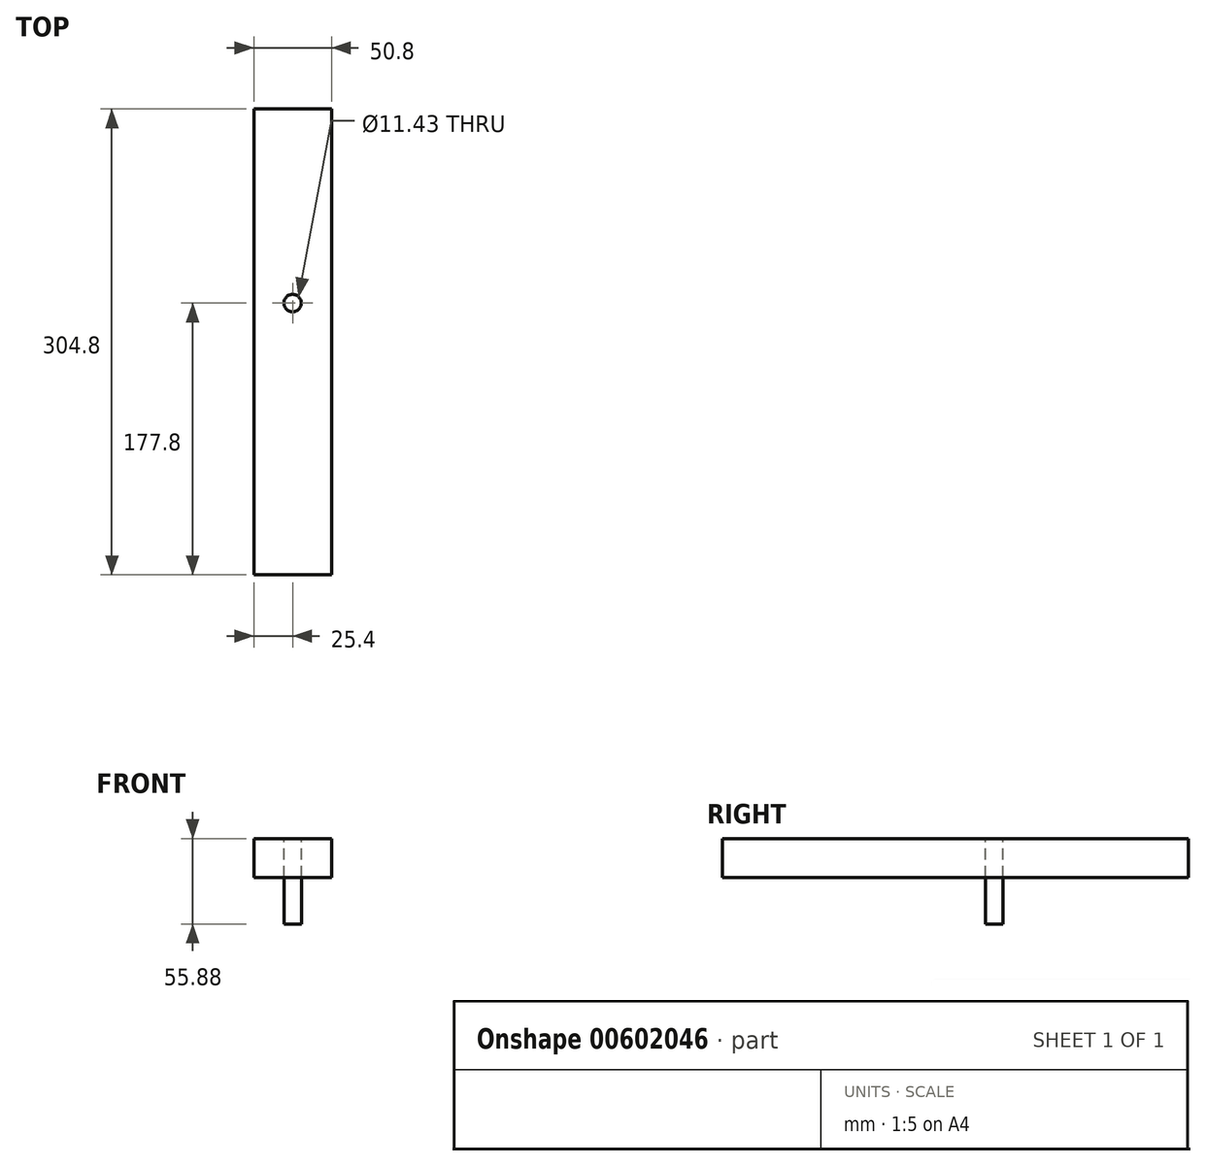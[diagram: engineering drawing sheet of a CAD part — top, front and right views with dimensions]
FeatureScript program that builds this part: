
annotation { "Feature Type Name" : "Feature", "Feature Type Description" : "" }
export const myFeature = defineFeature(function(context is Context, id is Id, definition is map)
    precondition{}
    {
        {
            var Q0;
            Q0=qCreatedBy(makeId("Front.planeOp"),FACE);
            var sketch = newSketch(context, id + "F0", { "sketchPlane" : qUnion([Q0])});
            skLineSegment(sketch, "E0.bottom", {"start": v(25.4, 12.7) * mm, "end": v(-25.4, 12.7) * mm});
            skLineSegment(sketch, "E0.top", {"start": v(25.4, -12.7) * mm, "end": v(-25.4, -12.7) * mm});
            skLineSegment(sketch, "E0.left", {"start": v(25.4, 12.7) * mm, "end": v(25.4, -12.7) * mm});
            skLineSegment(sketch, "E0.right", {"start": v(-25.4, 12.7) * mm, "end": v(-25.4, -12.7) * mm});
            skPoint(sketch, "E0.middle", {"position": v(0, 0) * mm});
            skSolve(sketch);
        }
        {
            var Q0;
            Q0 = qSketchRegion(id + "F0", true);
            extrude(context, id + "F1", {"entities" : qUnion([Q0]), "endBound" : BoundingType.SYMMETRIC, "depth" : 304.8 * mm, "offsetDistance" : 25.4 * mm, "hasSecondDirection" : true, "secondDirectionOppositeDirection" : true, "secondDirectionDepth" : 25.4 * mm});
        }
        {
            var Q0;
            Q0=makeQuery(id+"F1.opExtrude","SWEPT_FACE",FACE,{"disambiguationData":[OSD([sQuery(id+"F0.wireOp",EDGE,"E0.bottom")])]});
            var sketch = newSketch(context, id + "F2", { "sketchPlane" : qUnion([Q0])});
            skCircle(sketch, "E1", {"center": v(0, 25.4) * mm, "radius": 5.72 * mm});
            skPoint(sketch, "E1.centerSnap0", {"position": v(0, -152.4) * mm});
            skSolve(sketch);
        }
        {
            var Q0;
            Q0 = qSketchRegion(id + "F2", true);
            extrude(context, id + "F3", {"entities" : qUnion([Q0]), "operationType" : NewBodyOperationType.REMOVE, "endBound" : BoundingType.THROUGH_ALL, "oppositeDirection" : true, "depth" : 25.4 * mm, "offsetDistance" : 25.4 * mm});
        }
        {
            var Q0;
            Q0 = qSketchRegion(id + "F2", true);
            var Q1;
            Q1=makeQuery(id+"F1.opExtrude","SWEPT_FACE",FACE,{"disambiguationData":[OSD([sQuery(id+"F0.wireOp",EDGE,"E0.top")])]});
            extrude(context, id + "F4", {"entities" : qUnion([Q0]), "oppositeDirection" : true, "depth" : 55.88 * mm, "endBoundEntityFace" : qUnion([Q1]), "offsetDistance" : 25.4 * mm});
        }
    });
